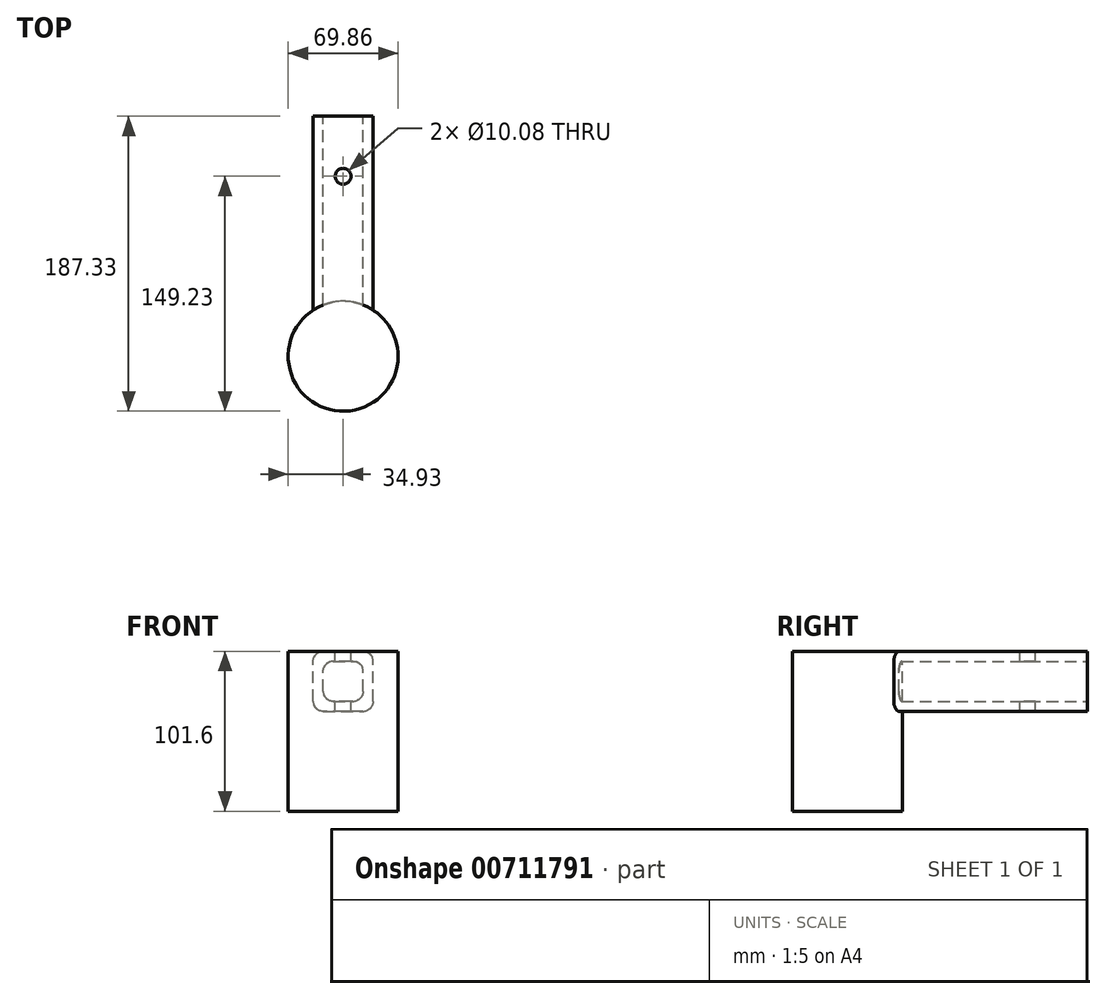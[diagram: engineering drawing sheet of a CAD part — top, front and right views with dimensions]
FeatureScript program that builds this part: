
annotation { "Feature Type Name" : "Feature", "Feature Type Description" : "" }
export const myFeature = defineFeature(function(context is Context, id is Id, definition is map)
    precondition{}
    {
        {
            var Q0;
            Q0=qCreatedBy(makeId("Front.planeOp"),FACE);
            var sketch = newSketch(context, id + "F0", { "sketchPlane" : qUnion([Q0])});
            skLineSegment(sketch, "E0.bottom", {"start": v(6.35, 0) * mm, "end": v(31.75, 0) * mm});
            skLineSegment(sketch, "E0.top", {"start": v(6.35, 38.1) * mm, "end": v(31.75, 38.1) * mm});
            skLineSegment(sketch, "E0.left", {"start": v(0, 6.35) * mm, "end": v(0, 31.75) * mm});
            skLineSegment(sketch, "E0.right", {"start": v(38.1, 6.35) * mm, "end": v(38.1, 31.75) * mm});
            skLineSegment(sketch, "E1.bottom", {"start": v(12.7, 6.35) * mm, "end": v(25.4, 6.35) * mm});
            skLineSegment(sketch, "E1.top", {"start": v(12.7, 31.75) * mm, "end": v(25.4, 31.75) * mm});
            skLineSegment(sketch, "E1.left", {"start": v(6.35, 12.7) * mm, "end": v(6.35, 25.4) * mm});
            skLineSegment(sketch, "E1.right", {"start": v(31.75, 12.7) * mm, "end": v(31.75, 25.4) * mm});
            skPoint(sketch, "E2.visualSharp", {"position": v(38.1, 38.1) * mm});
            skArc(sketch, "E2.filletArc", {"start": v(38.1, 31.75) * mm, "mid": v(36.24, 36.24) * mm, "end": v(31.75, 38.1) * mm});
            skPoint(sketch, "E3.visualSharp", {"position": v(38.1, 0) * mm});
            skArc(sketch, "E3.filletArc", {"start": v(31.75, 0) * mm, "mid": v(36.24, 1.86) * mm, "end": v(38.1, 6.35) * mm});
            skPoint(sketch, "E4.visualSharp", {"position": v(0, 0) * mm});
            skArc(sketch, "E4.filletArc", {"start": v(0, 6.35) * mm, "mid": v(1.86, 1.86) * mm, "end": v(6.35, 0) * mm});
            skPoint(sketch, "E5.visualSharp", {"position": v(0, 38.1) * mm});
            skArc(sketch, "E5.filletArc", {"start": v(6.35, 38.1) * mm, "mid": v(1.86, 36.24) * mm, "end": v(0, 31.75) * mm});
            skArc(sketch, "E6.filletArc", {"start": v(12.7, 31.75) * mm, "mid": v(8.2, 29.9) * mm, "end": v(6.35, 25.4) * mm});
            skArc(sketch, "E7.filletArc", {"start": v(25.4, 6.35) * mm, "mid": v(29.9, 8.2) * mm, "end": v(31.75, 12.7) * mm});
            skArc(sketch, "E8.filletArc", {"start": v(31.75, 25.4) * mm, "mid": v(29.9, 29.9) * mm, "end": v(25.4, 31.75) * mm});
            skArc(sketch, "E9.filletArc", {"start": v(6.35, 12.7) * mm, "mid": v(8.2, 8.2) * mm, "end": v(12.7, 6.35) * mm});
            skSolve(sketch);
        }
        {
            var Q0;
            Q0 = qSketchRegion(id + "F0", true);
            extrude(context, id + "F1", {"entities" : qUnion([Q0]), "depth" : 152.4 * mm, "offsetDistance" : 25.4 * mm});
        }
        {
            var Q0;
            Q0=makeQuery(id+"F1.opExtrude","SWEPT_FACE",FACE,{"disambiguationData":[OSD([sQuery(id+"F0.wireOp",EDGE,"E0.top")])]});
            var sketch = newSketch(context, id + "F2", { "sketchPlane" : qUnion([Q0])});
            skCircle(sketch, "E10", {"center": v(19.05, -152.4) * mm, "radius": 34.93 * mm});
            skSolve(sketch);
        }
        {
            var Q0;
            Q0 = qSketchRegion(id + "F2", true);
            extrude(context, id + "F3", {"entities" : qUnion([Q0]), "operationType" : NewBodyOperationType.ADD, "oppositeDirection" : true, "depth" : 101.6 * mm, "offsetDistance" : 25.4 * mm});
        }
        {
            var Q0;
            Q0=makeQuery(id+"F3.boolean.opBoolean","MERGE",FACE,{"derivedFrom":[makeQuery(id+"F1.opExtrude","SWEPT_FACE",FACE,{"disambiguationData":[OSD([sQuery(id+"F0.wireOp",EDGE,"E0.top")])]}),makeQuery(id+"F3.opExtrude","CAP_FACE",FACE,{"disambiguationData":[OSD([sQuery(id+"F2.wireOp",EDGE,"E10")])],"isStart":true})]});
            var sketch = newSketch(context, id + "F4", { "sketchPlane" : qUnion([Q0])});
            skPoint(sketch, "E11", {"position": v(19.05, -38.1) * mm});
            skPoint(sketch, "E11.positionSnap0", {"position": v(19.05, 0) * mm});
            skSolve(sketch);
        }
        {
            var Q0;
            Q0=sQuery(id+"F4.wireOp",VERTEX,"E11");
            var Q1;
            Q1=makeQuery(id+"F1.opExtrude","SWEPT_BODY",BODY,{"disambiguationData":[OSD([sQuery(id+"F0.wireOp",EDGE,"E0.bottom"),sQuery(id+"F0.wireOp",EDGE,"E0.top"),sQuery(id+"F0.wireOp",EDGE,"E0.left"),sQuery(id+"F0.wireOp",EDGE,"E0.right"),sQuery(id+"F0.wireOp",EDGE,"E1.bottom"),sQuery(id+"F0.wireOp",EDGE,"E1.top"),sQuery(id+"F0.wireOp",EDGE,"E1.left"),sQuery(id+"F0.wireOp",EDGE,"E1.right"),sQuery(id+"F0.wireOp",EDGE,"E2.filletArc"),sQuery(id+"F0.wireOp",EDGE,"E3.filletArc"),sQuery(id+"F0.wireOp",EDGE,"E4.filletArc"),sQuery(id+"F0.wireOp",EDGE,"E5.filletArc"),sQuery(id+"F0.wireOp",EDGE,"E6.filletArc"),sQuery(id+"F0.wireOp",EDGE,"E7.filletArc"),sQuery(id+"F0.wireOp",EDGE,"E8.filletArc"),sQuery(id+"F0.wireOp",EDGE,"E9.filletArc")])]});
            hole(context, id + "F5", {"style" : HoleStyle.SIMPLE, "endStyle" : HoleEndStyle.THROUGH, "standardTappedOrClearance" : lookupTablePath({ "standard" : "ANSI", "fit" : "Normal (ASME)", "size" : "3/8", "type" : "Clearance" }), "standardBlindInLast" : lookupTablePath({ "fit" : "Free", "standard" : "ANSI", "size" : "3/8", "type" : "Clearance" }), "holeDiameter" : 10.08 * mm, "majorDiameter" : 9.52 * mm, "tappedDepth" : 20.64 * mm, "tapClearance" : 3, "startFromSketch" : true, "locations" : qUnion([Q0]), "scope" : qUnion([Q1])});
        }
    });
